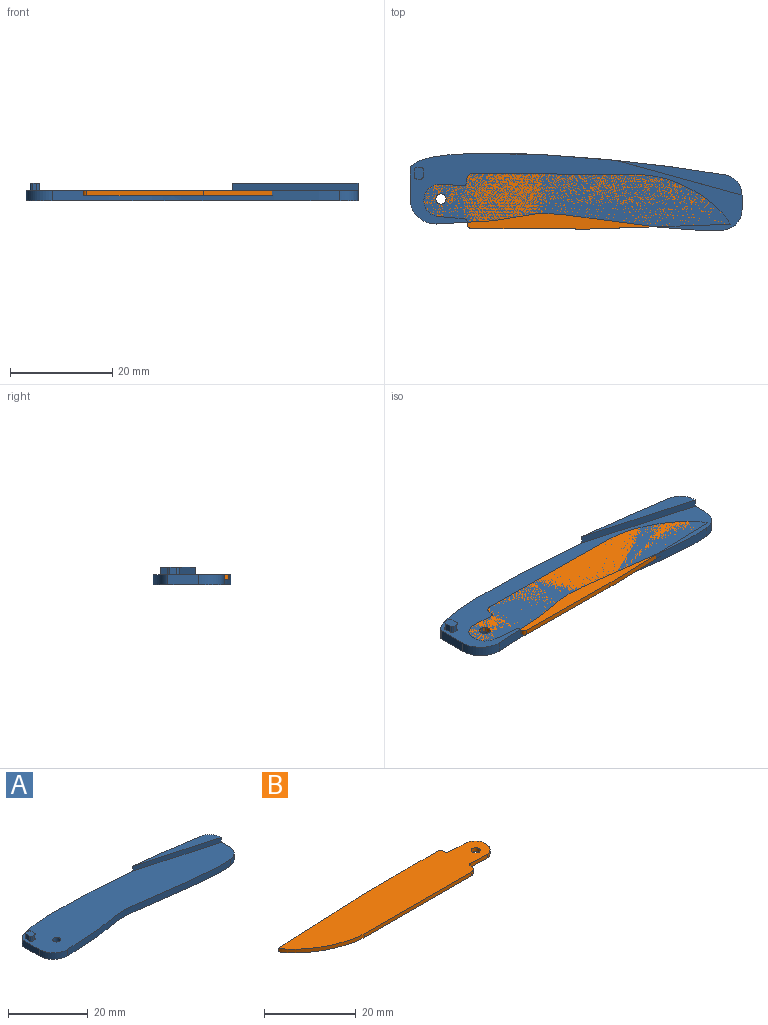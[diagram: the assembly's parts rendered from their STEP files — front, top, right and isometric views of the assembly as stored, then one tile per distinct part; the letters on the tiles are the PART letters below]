
ASSEMBLY  parts=2 mates=1
PART A: 21 faces, bbox 65x20x3.5 mm
  f0: plane 65x18.93mm, normal (0,0,1), area 729mm2, adj f1,f2,f3,f4,f5,f7,f9,f10
  f1: plane 5.99x2mm, normal (-1,0,0), area 12mm2, adj f0,f5,f6,f20
  f2: extruded ~56.34x3.37mm, area 113.4mm2, adj f0,f6,f7,f20
  f3: plane 2.87x2mm, normal (1,0,0), area 5.7mm2, adj f0,f6,f7,f8
  f4: cylinder r=1mm len=2mm, axis (0,0,-1), area 12.6mm2, adj f0,f6
  f5: extruded ~61.69x4.28mm, area 157.3mm2, adj f0,f1,f6,f8,f18,f19
  f6: plane 65x20mm, normal (0,0,-1), area 775.9mm2, adj f1,f2,f3,f4,f5,f7,f8,f20
  f7: cylinder r=4mm len=3.98mm, axis (0,0,-1), area 11.7mm2, adj f0,f2,f3,f6
  f8: cylinder r=4mm len=3.94mm, axis (0,0,-1), area 19.6mm2, adj f3,f5,f6,f18,f19
  f9: plane 1.5x0.76mm, normal (0,1,0), area 1.1mm2, adj f0,f13,f14,f17
  f10: plane 1.5x1.3mm, normal (-1,0,0), area 1.9mm2, adj f0,f13,f14,f15
  f11: plane 1.5x0.76mm, normal (0,-1,0), area 1.1mm2, adj f0,f13,f15,f16
  f12: plane 1.5x1.3mm, normal (1,0,0), area 1.9mm2, adj f0,f13,f16,f17
  f13: plane 2.3x1.76mm, normal (0,0,1), area 3.8mm2, adj f9,f10,f11,f12,f14,f15,f16,f17
  f14: cylinder r=0.5mm len=1.5mm, axis (0,0,-1), area 1.2mm2, adj f0,f9,f10,f13
  f15: cylinder r=0.5mm len=1.5mm, axis (0,0,-1), area 1.2mm2, adj f0,f10,f11,f13
  f16: cylinder r=0.5mm len=1.5mm, axis (0,0,-1), area 1.2mm2, adj f0,f11,f12,f13
  f17: cylinder r=0.5mm len=1.5mm, axis (0,0,-1), area 1.2mm2, adj f0,f9,f12,f13
  f18: plane 24.54x6.78mm, normal (-0.27,-0.96,0), area 38.2mm2, adj f0,f5,f8,f19
  f19: plane 24.73x6.96mm, normal (0,0,1), area 43.1mm2, adj f5,f8,f18
  f20: cylinder r=5mm len=5.1mm, axis (0,0,-1), area 15.9mm2, adj f0,f1,f2,f6
PART B: 17 faces, bbox 60x10.8x1 mm
  f0: plane 33.07x1mm, normal (0,-1,0), area 33.1mm2, adj f1,f14,f15,f16
  f1: cylinder r=1.5mm len=1.5mm, axis (0,0,-1), area 2.3mm2, adj f0,f2,f15,f16
  f2: plane 1x0.51mm, normal (1,-0.04,0), area 0.5mm2, adj f1,f3,f15,f16
  f3: cylinder r=0.5mm len=1mm, axis (0,0,-1), area 0.9mm2, adj f2,f4,f15,f16
  f4: plane 5.14x1mm, normal (-0.03,-1,0), area 5.1mm2, adj f3,f5,f15,f16
  f5: cylinder r=3.04mm len=3.07mm, axis (0,0,-1), area 4.3mm2, adj f4,f6,f15,f16
  f6: cylinder r=3mm len=3.2mm, axis (0,0,-1), area 4.7mm2, adj f5,f7,f15,f16
  f7: plane 5.14x1mm, normal (0.08,1,0), area 5.2mm2, adj f6,f8,f15,f16
  f8: cylinder r=0.71mm len=1mm, axis (0,0,-1), area 1.1mm2, adj f7,f9,f15,f16
  f9: plane 1x0.4mm, normal (1,0,0), area 0.4mm2, adj f8,f10,f15,f16
  f10: cylinder r=0.68mm len=1mm, axis (0,0,-1), area 1.1mm2, adj f9,f11,f15,f16
  f11: plane 22.9x1mm, normal (0,1,0), area 22.9mm2, adj f10,f12,f15,f16
  f12: plane 27.88x1.21mm, normal (-0.04,1,0), area 27.9mm2, adj f11,f14,f15,f16
  f13: cylinder r=1mm len=2mm, axis (0,0,-1), area 6.3mm2, adj f15,f16
  f14: extruded ~17.16x9.51mm, area 20.3mm2, adj f0,f12,f15,f16
  f15: plane 60.01x10.8mm, normal (0,0,1), area 532mm2, adj f0,f1,f2,f3,f4,f5,f6,f7
  f16: plane 60.01x10.8mm, normal (0,0,-1), area 532mm2, adj f0,f1,f2,f3,f4,f5,f6,f7
PLACE A t=(-13.88,6.1,-15.04)mm fixed
PLACE B rot(axis=(0,0,1),179.4deg) t=(48.91,16.01,-14.04)mm
MATE revolute B.f13 <-> A.f4  axis (0,0,1) through (-7.81,11.04,-13.04)mm
